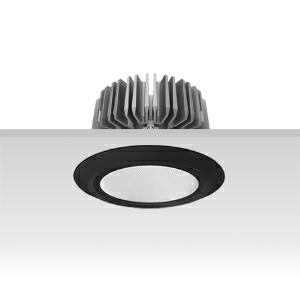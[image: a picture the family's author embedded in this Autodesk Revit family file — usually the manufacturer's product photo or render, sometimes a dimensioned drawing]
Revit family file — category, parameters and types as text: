
# Revit family: 3f_filippi_-_3f_reno_bianco_ampio_3f_filippi_-_30353_a01036_-_3f_reno_150_wh_3000-930_wide___vs_bk_d134
name_source: partatom
category: Lighting Fixtures
units: mm (PartAtom-declared; Revit-internal decimal feet)

## family parameters
Cut with Voids When Loaded = No
Host = Face
Light Source = No
Part Type = Normal
Room Calculation Point = No
Round Connector Dimension = Use Diameter
Shared = No

## types (1)
- 3F Filippi - 3F Reno Bianco Ampio (1 x LED, 2301 lm, 37 W, 3000 K)
    Apparent Load = 37 VA
    Approval mark = CE
    CIE Flux Codes = 74 93 99 100 100
    Color Rendering = 90
    Color Temperature = 3000 K
    Control Gear = Electronic ballast
    Default Elevation = 1800 mm
    Description = ILLUMINOTECHNICAL
Luminous efficiency 100% (DLOR 100%, ULOR 0%).
Initial luminous flux of the luminaire 2301 lm.
Direct symmetric wide distribution.
Installation Interdistance Transv.D = 1.12 x hu - Long.D = 1.11 x hu.
Tabular UGR (CIE 117 - 4H-8H; S=0.25H; 70/50/20): RUG 23.9 - 23.7.
Beam angle: 74° - 73°.
Luminous efficacy 62 lm/W.
Lifetime (L90/B10): 30000 h. (tq+25°C)
Lifetime (L85/B10): 50000 h. (tq+25°C)
Lifetime (L70/B10): 80000 h. (tq+25°C)
Sudden decreased luminous flux after 50000 hours: 0% (C0).
Photobiological safety in compliance with IEC/TR 62778: RG0 risk exempt, (IEC 62471).
In compliance with IEC/EN 62722-2-1 - IEC/EN 62717 standards.

SOURCE
Compact LED module 3000/930.
Energy efficiency class (UE 2019/2020 - UE 2019/2015): E.
CIE 13.3 Colour rendering index: CRI >90 (R9 >50%).
IES TM-30 Fidelity Index: Rf = 92 Rg = 101.
CCT nominal colour temperature 3000 K.
Colour initial tolerance (MacAdam): SDCM 3.
Zhaga Book 3 compliant.

MECHANICAL
Passive heat dissipator in die-casting aluminium, oversized, for optimum thermal management of the LED module.
Parabolic element with graduated/concentric rings in white polycarbonate.
Transparent external lens with glossy and satin differentiated surfaces, with a cooling and anti-insect system in methacrylate (PMMA).
Fastening spring clips in stainless steel.
Dimensions: diameter 176 mm, height 111 mm. Weight 1.455 kg.
IP44 protection degree for exposed part, IP20 for recessed part.
Mechanical strength to impacts IK06 (1 joule).
Glow-wire test resistance 650°C.

ELECTRICAL
Wiring on a separate unit.
Halogen Free electronic wiring 230V-50/60Hz, power factor 0.95, THD <25%, constant output current, SELV, class II, 1 driver.
Power of the luminaire 37 W.
ENEC - CE.
SAFE FLICKER: PstLM=<1 and SVM=<0.4 (IEC TR 61547-1 and IEC TR 63158), to ensure a more comfortable and safe light.
Luminaire compliant with EN 60598-2-22 for power supply from a centralised emergency system CPSS (Central Power Supply System), not incorporated in the luminaire - high risk areas excluded. The default power and flux are 100% in AC and 100% in DC.
Ambient temperature from 0°C to +25°C.
Temperature class T6 max 85°C.
Relative humidity UR: <85%.

INSTALLATION
Pull-up recessed fitting.
False ceiling carving: 150 mm.
All accessories dedicated to this product are available on the Catalog and on our website www.3F-Filippi.com.

ACCESSORIES
A01036 - Anti-glare microprismatic VS moulded glass, tempered, not flammable, locked and in line with the trim, in black polycarbonate.

APPLICATIONS
Environments: architectural, commercial, exhibition areas, transit areas, corridors, shops, display windows, service areas.
In false ceilings with narrow voids.

WARNING
Luminaire designed for disposal/recycling at end-of-life.
Replaceable (LED only) light source by a professional. Replaceable control gear by a professional.
    Height = 0 mm  [stored 0 ft]
    Lamp = 1 x LED
    Lamp Light Flux = 2301 lm
    Lamp Power = 37 W
    Lamp count = 1
    Length = 176 mm
    Lifetime = 50000 h
    Luminous efficacy = 62 lm/W
    Manufacturer = 3F Filippi
    ModVariant = No
    Model = 3F Filippi - 30353+A01036 - 3F Reno 150 WH 3000-930 WIDE + VS BK
    Mounting Place = Ceiling
    Mounting Type = Recessed
    Number of Poles = 1
    OnlyDefault = Yes
    Power Factor = 1
    Product Name = 3F Filippi - 3F Reno Bianco Ampio
    Product group = recessed luminaire
    ProductGroupID = 4
    Protection Class = Protection class II
    Protection Degree = IP 20
    RLX_Detail_Level = 1
    RLX_Emergency_Light_Flux = 0 lm
    RLX_Emergency_Type = 0
    RLX_Emergency_Type_DB = No
    RlxData = <blob elided: 86157 chars, md5=542a427a>
    Socket = socket
    Standby Power = 0 W
    System Light Flux = 2301 lm
    System Power = 37 W
    Type Comments = Product without accessories
    Type Image = 3ffilippi_3f_reno_150_bk_vs_smp.jpg
    URL = http://relux.com
    VarID = ---
    Voltage = 0 V
    Weight = 0.00 kg
    Width = 0 mm  [stored 0 ft]

note: [stored X ft] marks values corroborated as IEEE doubles in the binary element streams (Revit-internal decimal feet)

## geometry (parser evidence)
native form markers: Blend x4, Sweep x11
no freeform markers — native parametric forms only
